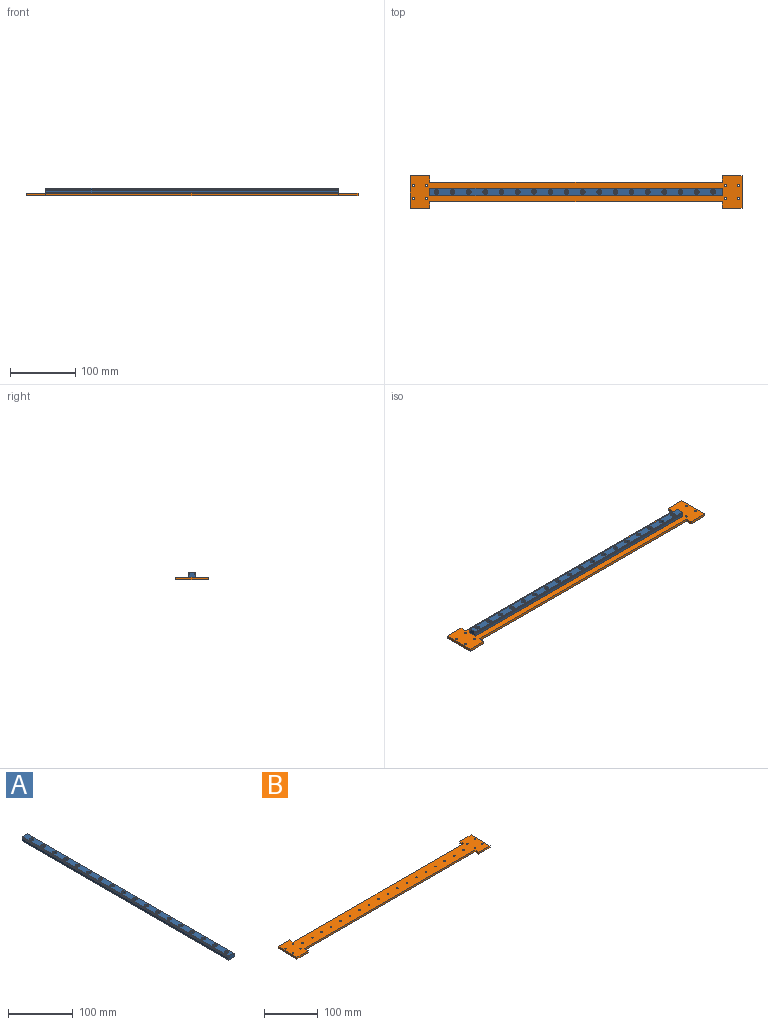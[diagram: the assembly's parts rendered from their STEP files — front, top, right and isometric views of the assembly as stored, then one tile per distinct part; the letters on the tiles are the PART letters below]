
ASSEMBLY  parts=2 mates=1
PART A: 120 faces, bbox 12x450x8 mm
  f0: cone r=3mm half-angle=45deg, axis (0,0,1), area 14.4mm2, adj f3,f105
  f1: cone r=1.75mm half-angle=45deg, axis (0,0,-1), area 8.9mm2, adj f2,f91
  f2: cylinder r=1.75mm len=3.5mm, axis (0,0,1), area 33mm2, adj f1,f4
  f3: cylinder r=3mm len=6mm, axis (0,0,1), area 75.4mm2, adj f0,f4
  f4: plane 6x6mm, normal (0,0,1), area 18.7mm2, adj f2,f3
  f5: cone r=3mm half-angle=45deg, axis (0,0,1), area 14.4mm2, adj f8,f105
  f6: cone r=1.75mm half-angle=45deg, axis (0,0,-1), area 8.9mm2, adj f7,f91
  f7: cylinder r=1.75mm len=3.5mm, axis (0,0,1), area 33mm2, adj f6,f9
  f8: cylinder r=3mm len=6mm, axis (0,0,1), area 75.4mm2, adj f5,f9
  f9: plane 6x6mm, normal (0,0,1), area 18.7mm2, adj f7,f8
  f10: cone r=3mm half-angle=45deg, axis (0,0,1), area 14.4mm2, adj f13,f105
  f11: cone r=1.75mm half-angle=45deg, axis (0,0,-1), area 8.9mm2, adj f12,f91
  f12: cylinder r=1.75mm len=3.5mm, axis (0,0,1), area 33mm2, adj f11,f14
  f13: cylinder r=3mm len=6mm, axis (0,0,1), area 75.4mm2, adj f10,f14
  f14: plane 6x6mm, normal (0,0,1), area 18.7mm2, adj f12,f13
  f15: cone r=3mm half-angle=45deg, axis (0,0,1), area 14.4mm2, adj f18,f105
  f16: cone r=1.75mm half-angle=45deg, axis (0,0,-1), area 8.9mm2, adj f17,f91
  f17: cylinder r=1.75mm len=3.5mm, axis (0,0,1), area 33mm2, adj f16,f19
  f18: cylinder r=3mm len=6mm, axis (0,0,1), area 75.4mm2, adj f15,f19
  f19: plane 6x6mm, normal (0,0,1), area 18.7mm2, adj f17,f18
  f20: cone r=3mm half-angle=45deg, axis (0,0,1), area 14.4mm2, adj f23,f105
  f21: cone r=1.75mm half-angle=45deg, axis (0,0,-1), area 8.9mm2, adj f22,f91
  f22: cylinder r=1.75mm len=3.5mm, axis (0,0,1), area 33mm2, adj f21,f24
  f23: cylinder r=3mm len=6mm, axis (0,0,1), area 75.4mm2, adj f20,f24
  f24: plane 6x6mm, normal (0,0,1), area 18.7mm2, adj f22,f23
  f25: cone r=3mm half-angle=45deg, axis (0,0,1), area 14.4mm2, adj f28,f105
  f26: cone r=1.75mm half-angle=45deg, axis (0,0,-1), area 8.9mm2, adj f27,f91
  f27: cylinder r=1.75mm len=3.5mm, axis (0,0,1), area 33mm2, adj f26,f29
  f28: cylinder r=3mm len=6mm, axis (0,0,1), area 75.4mm2, adj f25,f29
  f29: plane 6x6mm, normal (0,0,1), area 18.7mm2, adj f27,f28
  f30: cone r=3mm half-angle=45deg, axis (0,0,1), area 14.4mm2, adj f33,f105
  f31: cone r=1.75mm half-angle=45deg, axis (0,0,-1), area 8.9mm2, adj f32,f91
  f32: cylinder r=1.75mm len=3.5mm, axis (0,0,1), area 33mm2, adj f31,f34
  f33: cylinder r=3mm len=6mm, axis (0,0,1), area 75.4mm2, adj f30,f34
  f34: plane 6x6mm, normal (0,0,1), area 18.7mm2, adj f32,f33
  f35: cone r=3mm half-angle=45deg, axis (0,0,1), area 14.4mm2, adj f38,f105
  f36: cone r=1.75mm half-angle=45deg, axis (0,0,-1), area 8.9mm2, adj f37,f91
  f37: cylinder r=1.75mm len=3.5mm, axis (0,0,1), area 33mm2, adj f36,f39
  f38: cylinder r=3mm len=6mm, axis (0,0,1), area 75.4mm2, adj f35,f39
  f39: plane 6x6mm, normal (0,0,1), area 18.7mm2, adj f37,f38
  f40: cone r=3mm half-angle=45deg, axis (0,0,1), area 14.4mm2, adj f43,f105
  f41: cone r=1.75mm half-angle=45deg, axis (0,0,-1), area 8.9mm2, adj f42,f91
  f42: cylinder r=1.75mm len=3.5mm, axis (0,0,1), area 33mm2, adj f41,f44
  f43: cylinder r=3mm len=6mm, axis (0,0,1), area 75.4mm2, adj f40,f44
  f44: plane 6x6mm, normal (0,0,1), area 18.7mm2, adj f42,f43
  f45: cone r=3mm half-angle=45deg, axis (0,0,1), area 14.4mm2, adj f48,f105
  f46: cone r=1.75mm half-angle=45deg, axis (0,0,-1), area 8.9mm2, adj f47,f91
  f47: cylinder r=1.75mm len=3.5mm, axis (0,0,1), area 33mm2, adj f46,f49
  f48: cylinder r=3mm len=6mm, axis (0,0,1), area 75.4mm2, adj f45,f49
  f49: plane 6x6mm, normal (0,0,1), area 18.7mm2, adj f47,f48
  f50: cone r=3mm half-angle=45deg, axis (0,0,1), area 14.4mm2, adj f53,f105
  f51: cone r=1.75mm half-angle=45deg, axis (0,0,-1), area 8.9mm2, adj f52,f91
  f52: cylinder r=1.75mm len=3.5mm, axis (0,0,1), area 33mm2, adj f51,f54
  f53: cylinder r=3mm len=6mm, axis (0,0,1), area 75.4mm2, adj f50,f54
  f54: plane 6x6mm, normal (0,0,1), area 18.7mm2, adj f52,f53
  f55: cone r=3mm half-angle=45deg, axis (0,0,1), area 14.4mm2, adj f58,f105
  f56: cone r=1.75mm half-angle=45deg, axis (0,0,-1), area 8.9mm2, adj f57,f91
  f57: cylinder r=1.75mm len=3.5mm, axis (0,0,1), area 33mm2, adj f56,f59
  f58: cylinder r=3mm len=6mm, axis (0,0,1), area 75.4mm2, adj f55,f59
  f59: plane 6x6mm, normal (0,0,1), area 18.7mm2, adj f57,f58
  f60: cone r=3mm half-angle=45deg, axis (0,0,1), area 14.4mm2, adj f63,f105
  f61: cone r=1.75mm half-angle=45deg, axis (0,0,-1), area 8.9mm2, adj f62,f91
  f62: cylinder r=1.75mm len=3.5mm, axis (0,0,1), area 33mm2, adj f61,f64
  f63: cylinder r=3mm len=6mm, axis (0,0,1), area 75.4mm2, adj f60,f64
  f64: plane 6x6mm, normal (0,0,1), area 18.7mm2, adj f62,f63
  f65: cone r=3mm half-angle=45deg, axis (0,0,1), area 14.4mm2, adj f68,f105
  f66: cone r=1.75mm half-angle=45deg, axis (0,0,-1), area 8.9mm2, adj f67,f91
  f67: cylinder r=1.75mm len=3.5mm, axis (0,0,1), area 33mm2, adj f66,f69
  f68: cylinder r=3mm len=6mm, axis (0,0,1), area 75.4mm2, adj f65,f69
  f69: plane 6x6mm, normal (0,0,1), area 18.7mm2, adj f67,f68
  f70: cone r=3mm half-angle=45deg, axis (0,0,1), area 14.4mm2, adj f73,f105
  f71: cone r=1.75mm half-angle=45deg, axis (0,0,-1), area 8.9mm2, adj f72,f91
  f72: cylinder r=1.75mm len=3.5mm, axis (0,0,1), area 33mm2, adj f71,f74
  f73: cylinder r=3mm len=6mm, axis (0,0,1), area 75.4mm2, adj f70,f74
  f74: plane 6x6mm, normal (0,0,1), area 18.7mm2, adj f72,f73
  f75: cone r=3mm half-angle=45deg, axis (0,0,1), area 14.4mm2, adj f78,f105
  f76: cone r=1.75mm half-angle=45deg, axis (0,0,-1), area 8.9mm2, adj f77,f91
  f77: cylinder r=1.75mm len=3.5mm, axis (0,0,1), area 33mm2, adj f76,f79
  f78: cylinder r=3mm len=6mm, axis (0,0,1), area 75.4mm2, adj f75,f79
  f79: plane 6x6mm, normal (0,0,1), area 18.7mm2, adj f77,f78
  f80: cone r=3mm half-angle=45deg, axis (0,0,1), area 14.4mm2, adj f83,f105
  f81: cone r=1.75mm half-angle=45deg, axis (0,0,-1), area 8.9mm2, adj f82,f91
  f82: cylinder r=1.75mm len=3.5mm, axis (0,0,1), area 33mm2, adj f81,f84
  f83: cylinder r=3mm len=6mm, axis (0,0,1), area 75.4mm2, adj f80,f84
  f84: plane 6x6mm, normal (0,0,1), area 18.7mm2, adj f82,f83
  f85: plane 450x0.42mm, normal (0,0,1), area 189.8mm2, adj f86,f112,f113,f114
  f86: cylinder r=0.16mm len=450mm, axis (0,-1,0), area 76.3mm2, adj f85,f87,f113,f114
  f87: cylinder r=1.14mm len=450mm, axis (0,-1,0), area 281.9mm2, adj f86,f88,f113,f114
  f88: cylinder r=0.16mm len=450mm, axis (0,-1,0), area 76.3mm2, adj f87,f89,f113,f114
  f89: plane 450x3.82mm, normal (-1,0,0), area 1719.8mm2, adj f88,f90,f113,f114
  f90: plane 450x0.5mm, normal (-0.71,0,-0.71), area 318.2mm2, adj f89,f91,f113,f114
  f91: plane 450x11mm, normal (0,0,-1), area 4663.7mm2, adj f1,f6,f11,f16,f21,f26,f31,f36
  f92: plane 450x0.5mm, normal (0.71,0,-0.71), area 318.2mm2, adj f91,f93,f113,f114
  f93: plane 450x3.82mm, normal (1,0,0), area 1719.8mm2, adj f92,f94,f113,f114
  f94: cylinder r=0.16mm len=450mm, axis (0,-1,0), area 76.3mm2, adj f93,f95,f113,f114
  f95: cylinder r=1.14mm len=450mm, axis (0,-1,0), area 281.9mm2, adj f94,f96,f113,f114
  f96: cylinder r=0.16mm len=450mm, axis (0,-1,0), area 76.3mm2, adj f95,f97,f113,f114
  f97: plane 450x0.42mm, normal (0,0,1), area 189.8mm2, adj f96,f98,f113,f114
  f98: cylinder r=0.5mm len=450mm, axis (0,-1,0), area 848.8mm2, adj f97,f99,f113,f114
  f99: plane 450x0.42mm, normal (0,0,-1), area 189.8mm2, adj f98,f100,f113,f114
  f100: cylinder r=0.16mm len=450mm, axis (0,-1,0), area 76.3mm2, adj f99,f101,f113,f114
  f101: cylinder r=1.14mm len=450mm, axis (0,-1,0), area 281.9mm2, adj f100,f102,f113,f114
  f102: cylinder r=0.16mm len=450mm, axis (0,-1,0), area 76.3mm2, adj f101,f103,f113,f114
  f103: plane 450x0.82mm, normal (1,0,0), area 369.8mm2, adj f102,f104,f113,f114
  f104: plane 450x0.59mm, normal (0.76,0,0.65), area 347.4mm2, adj f103,f105,f113,f114
  f105: plane 450x11mm, normal (0,0,1), area 4257.3mm2, adj f0,f5,f10,f15,f20,f25,f30,f35
  f106: plane 450x0.59mm, normal (-0.76,0,0.65), area 347.4mm2, adj f105,f107,f113,f114
  f107: plane 450x0.82mm, normal (-1,0,0), area 369.8mm2, adj f106,f108,f113,f114
  f108: cylinder r=0.16mm len=450mm, axis (0,-1,0), area 76.3mm2, adj f107,f109,f113,f114
  f109: cylinder r=1.14mm len=450mm, axis (0,-1,0), area 281.9mm2, adj f108,f110,f113,f114
  f110: cylinder r=0.16mm len=450mm, axis (0,-1,0), area 76.3mm2, adj f109,f111,f113,f114
  f111: plane 450x0.42mm, normal (0,0,-1), area 189.8mm2, adj f110,f112,f113,f114
  f112: cylinder r=0.5mm len=450mm, axis (0,-1,0), area 848.8mm2, adj f85,f111,f113,f114
  f113: plane 12x8mm, normal (0,1,0), area 91.5mm2, adj f85,f86,f87,f88,f89,f90,f91,f92
  f114: plane 12x8mm, normal (0,-1,0), area 91.5mm2, adj f85,f86,f87,f88,f89,f90,f91,f92
  f115: cylinder r=3mm len=6mm, axis (0,0,1), area 75.4mm2, adj f116,f119
  f116: plane 6x6mm, normal (0,0,1), area 18.7mm2, adj f115,f117
  f117: cylinder r=1.75mm len=3.5mm, axis (0,0,1), area 33mm2, adj f116,f118
  f118: cone r=1.75mm half-angle=45deg, axis (0,0,-1), area 8.9mm2, adj f91,f117
  f119: cone r=3mm half-angle=45deg, axis (0,0,1), area 14.4mm2, adj f105,f115
PART B: 40 faces, bbox 510x50x4 mm
  f0: cylinder r=1.5mm len=4mm, axis (0,0,1), area 37.7mm2, adj f28,f29
  f1: cylinder r=1.5mm len=4mm, axis (0,0,1), area 37.7mm2, adj f28,f29
  f2: cylinder r=1.5mm len=4mm, axis (0,0,1), area 37.7mm2, adj f28,f29
  f3: cylinder r=1.5mm len=4mm, axis (0,0,1), area 37.7mm2, adj f28,f29
  f4: cylinder r=1.5mm len=4mm, axis (0,0,1), area 37.7mm2, adj f28,f29
  f5: cylinder r=1.5mm len=4mm, axis (0,0,1), area 37.7mm2, adj f28,f29
  f6: cylinder r=1.5mm len=4mm, axis (0,0,1), area 37.7mm2, adj f28,f29
  f7: cylinder r=1.5mm len=4mm, axis (0,0,1), area 37.7mm2, adj f28,f29
  f8: cylinder r=1.5mm len=4mm, axis (0,0,1), area 37.7mm2, adj f28,f29
  f9: cylinder r=1.5mm len=4mm, axis (0,0,1), area 37.7mm2, adj f28,f29
  f10: cylinder r=1.5mm len=4mm, axis (0,0,1), area 37.7mm2, adj f28,f29
  f11: cylinder r=1.5mm len=4mm, axis (0,0,1), area 37.7mm2, adj f28,f29
  f12: cylinder r=1.5mm len=4mm, axis (0,0,1), area 37.7mm2, adj f28,f29
  f13: cylinder r=1.5mm len=4mm, axis (0,0,1), area 37.7mm2, adj f28,f29
  f14: cylinder r=1.5mm len=4mm, axis (0,0,1), area 37.7mm2, adj f28,f29
  f15: cylinder r=1.5mm len=4mm, axis (0,0,1), area 37.7mm2, adj f28,f29
  f16: cylinder r=1.5mm len=4mm, axis (0,0,1), area 37.7mm2, adj f28,f29
  f17: plane 30x4mm, normal (0,1,0), area 120mm2, adj f18,f27,f28,f29
  f18: plane 50x4mm, normal (-1,0,0), area 200mm2, adj f17,f19,f28,f29
  f19: plane 30x4mm, normal (0,-1,0), area 120mm2, adj f18,f20,f28,f29
  f20: plane 10x4mm, normal (1,0,0), area 40mm2, adj f19,f21,f28,f29
  f21: plane 450x4mm, normal (0,-1,0), area 1800mm2, adj f20,f28,f29,f33
  f22: plane 450x4mm, normal (0,1,0), area 1800mm2, adj f27,f28,f29,f38
  f23: cylinder r=1.5mm len=4mm, axis (0,0,-1), area 37.7mm2, adj f28,f29
  f24: cylinder r=1.5mm len=4mm, axis (0,0,-1), area 37.7mm2, adj f28,f29
  f25: cylinder r=1.5mm len=4mm, axis (0,0,-1), area 37.7mm2, adj f28,f29
  f26: cylinder r=1.5mm len=4mm, axis (0,0,-1), area 37.7mm2, adj f28,f29
  f27: plane 10x4mm, normal (1,0,0), area 40mm2, adj f17,f22,f28,f29
  f28: plane 510x50mm, normal (0,0,1), area 16316.2mm2, adj f0,f1,f2,f3,f4,f5,f6,f7
  f29: plane 510x50mm, normal (0,0,-1), area 16316.2mm2, adj f0,f1,f2,f3,f4,f5,f6,f7
  f30: plane 30x4mm, normal (0,1,0), area 120mm2, adj f28,f29,f31,f38
  f31: plane 50x4mm, normal (1,0,0), area 200mm2, adj f28,f29,f30,f32
  f32: plane 30x4mm, normal (0,-1,0), area 120mm2, adj f28,f29,f31,f33
  f33: plane 10x4mm, normal (-1,0,0), area 40mm2, adj f21,f28,f29,f32
  f34: cylinder r=1.5mm len=4mm, axis (0,0,-1), area 37.7mm2, adj f28,f29
  f35: cylinder r=1.5mm len=4mm, axis (0,0,-1), area 37.7mm2, adj f28,f29
  f36: cylinder r=1.5mm len=4mm, axis (0,0,-1), area 37.7mm2, adj f28,f29
  f37: cylinder r=1.5mm len=4mm, axis (0,0,-1), area 37.7mm2, adj f28,f29
  f38: plane 10x4mm, normal (-1,0,0), area 40mm2, adj f22,f28,f29,f30
  f39: cylinder r=1.5mm len=4mm, axis (0,0,1), area 37.7mm2, adj f28,f29
PLACE A rot(axis=(0,0,-1),90deg) t=(-210.15,7.54,4.88)mm
PLACE B t=(14.35,7.54,-3.12)mm
MATE fastened A.f115 <-> B.f39  axis (0,0,-1) through (-200.15,7.54,0.88)mm
